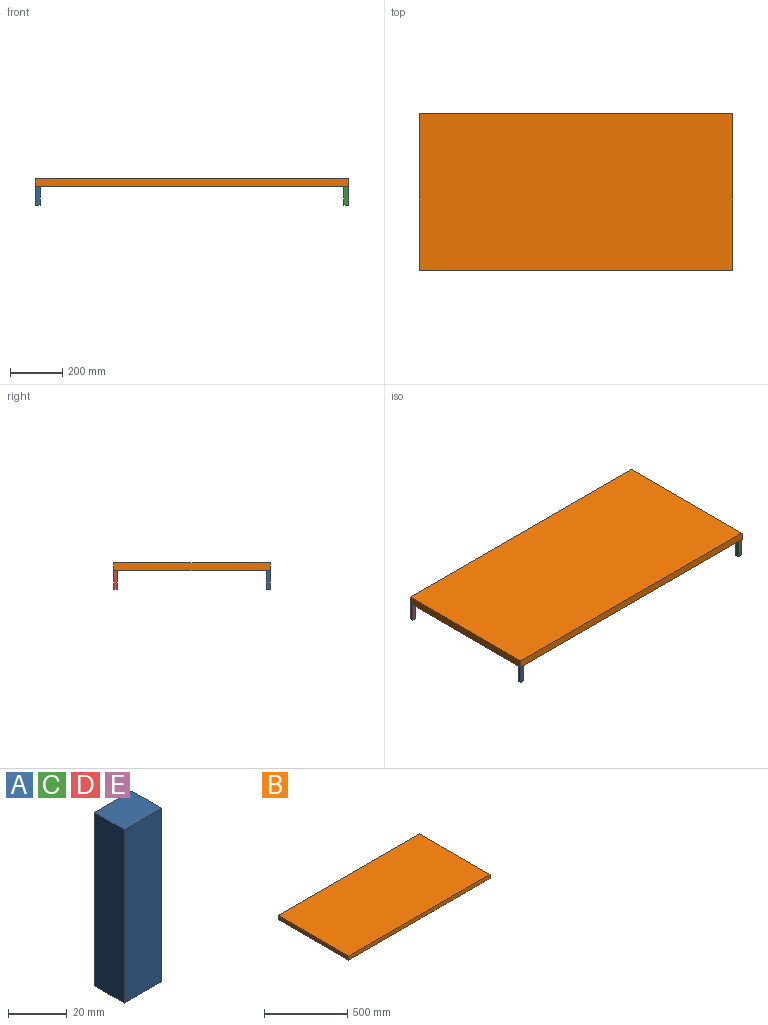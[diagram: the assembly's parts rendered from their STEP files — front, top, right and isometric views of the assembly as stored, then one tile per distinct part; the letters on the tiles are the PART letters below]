
ASSEMBLY  parts=5 mates=12
PART A: 6 faces, bbox 17.9x14.4x72 mm
  f0: plane 72x14.37mm, normal (-1,0,0), area 1034.4mm2, adj f1,f3,f4,f5
  f1: plane 72x17.87mm, normal (0,-1,0), area 1286.7mm2, adj f0,f2,f4,f5
  f2: plane 72x14.37mm, normal (1,0,0), area 1034.4mm2, adj f1,f3,f4,f5
  f3: plane 72x17.87mm, normal (0,1,0), area 1286.7mm2, adj f0,f2,f4,f5
  f4: plane 17.87x14.37mm, normal (0,0,1), area 256.7mm2, adj f0,f1,f2,f3
  f5: plane 17.87x14.37mm, normal (0,0,-1), area 256.7mm2, adj f0,f1,f2,f3
PART B: 6 faces, bbox 1200x600x30 mm
  f0: plane 600x30mm, normal (-1,0,0), area 18000mm2, adj f1,f3,f4,f5
  f1: plane 1200x30mm, normal (0,-1,0), area 36000mm2, adj f0,f2,f4,f5
  f2: plane 600x30mm, normal (1,0,0), area 18000mm2, adj f1,f3,f4,f5
  f3: plane 1200x30mm, normal (0,1,0), area 36000mm2, adj f0,f2,f4,f5
  f4: plane 1200x600mm, normal (0,0,1), area 720000mm2, adj f0,f1,f2,f3
  f5: plane 1200x600mm, normal (0,0,-1), area 720000mm2, adj f0,f1,f2,f3
PART C: same geometry as A
PART D: same geometry as A
PART E: same geometry as A
PLACE A t=(-149.34,-20.22,-78.63)mm
PLACE B t=(-48.95,26.77,-6.63)mm fixed
PLACE C t=(1032.79,-19.84,-78.63)mm
PLACE D t=(-149.34,565.41,-78.63)mm
PLACE E t=(1032.79,565.41,-78.63)mm
MATE planar B.f3 <-> D.f3  axis (0,1,0) through (384.42,504.06,8.37)mm
MATE planar B.f0 <-> A.f0  axis (-1,0,0) through (-215.58,204.06,8.37)mm
MATE planar B.f5 <-> A.f4  axis (0,0,-1) through (384.42,204.06,-6.63)mm
MATE planar B.f5 <-> E.f4  axis (0,0,1) through (984.42,504.06,-6.63)mm
MATE planar E.f4 <-> B.f5  axis (0,0,1) through (975.48,496.87,-6.63)mm
MATE planar E.f4 <-> B.f5  axis (0,0,1) through (966.55,504.06,-6.63)mm
MATE planar B.f1 <-> A.f1  axis (0,-1,0) through (384.42,-95.94,8.37)mm
MATE planar B.f0 <-> D.f0  axis (-1,0,0) through (-215.58,504.06,8.37)mm
MATE planar D.f4 <-> B.f5  axis (0,0,1) through (-206.65,496.87,-6.63)mm
MATE planar B.f4 <-> B.f5  axis (0,0,1) through (384.42,204.06,23.37)mm
MATE planar B.f5 <-> C.f4  axis (0,0,-1) through (384.42,204.06,-6.63)mm
MATE planar B.f2 <-> C.f2  axis (1,0,0) through (984.42,-95.94,8.37)mm
